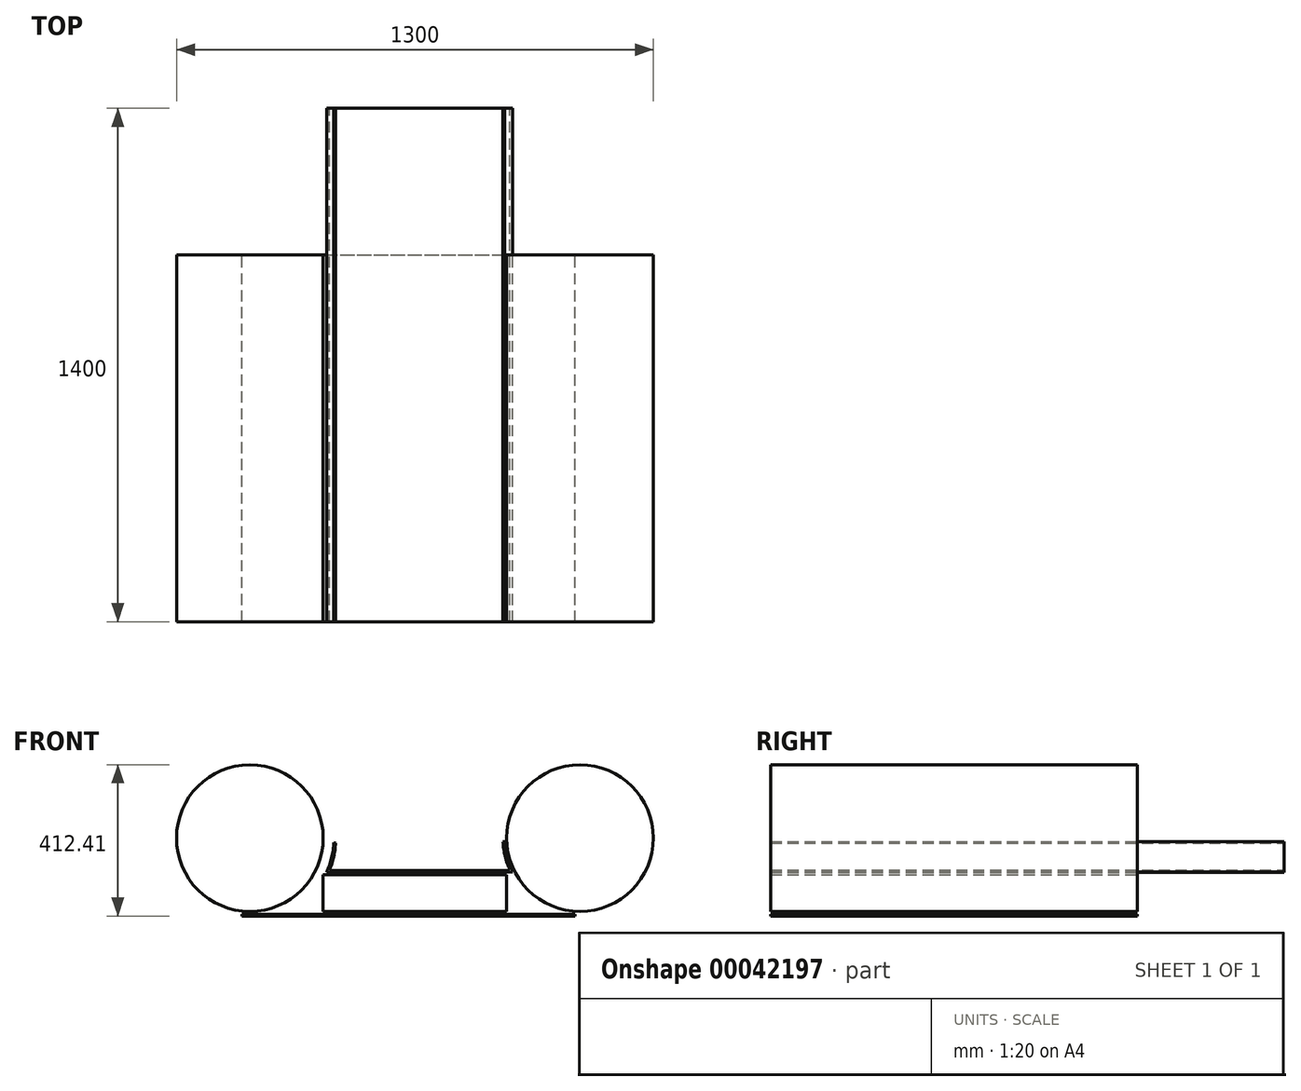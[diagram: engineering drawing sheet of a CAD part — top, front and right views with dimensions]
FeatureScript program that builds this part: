
annotation { "Feature Type Name" : "Feature", "Feature Type Description" : "" }
export const myFeature = defineFeature(function(context is Context, id is Id, definition is map)
    precondition{}
    {
        {
            var Q0;
            Q0=qCreatedBy(makeId("Front.planeOp"),FACE);
            var sketch = newSketch(context, id + "F0", { "sketchPlane" : qUnion([Q0])});
            skCircle(sketch, "E0", {"center": v(-531.07, -125.53) * mm, "radius": 200 * mm});
            skPoint(sketch, "E0.first.point", {"position": v(-686.77, 0) * mm});
            skPoint(sketch, "E0.second.point", {"position": v(-357.87, -225.53) * mm});
            skPoint(sketch, "E0.third.point", {"position": v(-531.07, -325.53) * mm});
            skLineSegment(sketch, "E1.bottom", {"start": v(-331.07, -225.53) * mm, "end": v(168.93, -225.53) * mm});
            skLineSegment(sketch, "E1.top", {"start": v(-331.07, -325.53) * mm, "end": v(168.93, -325.53) * mm});
            skLineSegment(sketch, "E1.left", {"start": v(-331.07, -225.53) * mm, "end": v(-331.07, -325.53) * mm});
            skLineSegment(sketch, "E1.right", {"start": v(168.93, -225.53) * mm, "end": v(168.93, -325.53) * mm});
            skLineSegment(sketch, "E2", {"start": v(-916.77, -325.53) * mm, "end": v(688.73, -325.53) * mm, "construction": true});
            skCircle(sketch, "E3", {"center": v(368.93, -125.53) * mm, "radius": 200 * mm});
            skPoint(sketch, "E3.first.point", {"position": v(267.48, 46.83) * mm});
            skPoint(sketch, "E3.second.point", {"position": v(368.93, -325.53) * mm});
            skPoint(sketch, "E3.third.point", {"position": v(168.93, -225.53) * mm});
            skArc(sketch, "E4", {"start": v(-321.78, -218.91) * mm, "mid": v(-308.32, -179.42) * mm, "end": v(-302.24, -138.14) * mm});
            skArc(sketch, "E5", {"start": v(164.15, -135.08) * mm, "mid": v(170.65, -177.6) * mm, "end": v(185.89, -217.84) * mm});
            skLineSegment(sketch, "E6", {"start": v(-321.78, -218.91) * mm, "end": v(185.89, -217.84) * mm});
            skArc(sketch, "E7.0", {"start": v(-314.2, -213.9) * mm, "mid": v(-302.59, -176.86) * mm, "end": v(-297.25, -138.41) * mm});
            skLineSegment(sketch, "E7.1", {"start": v(-314.2, -213.9) * mm, "end": v(177.94, -212.86) * mm});
            skArc(sketch, "E7.2", {"start": v(159.15, -135.31) * mm, "mid": v(164.83, -174.99) * mm, "end": v(177.94, -212.86) * mm});
            skLineSegment(sketch, "E8", {"start": v(-302.24, -138.14) * mm, "end": v(-297.25, -138.41) * mm});
            skLineSegment(sketch, "E9", {"start": v(159.15, -135.31) * mm, "end": v(164.15, -135.08) * mm});
            skLineSegment(sketch, "E10.bottom", {"start": v(-552.84, -333.33) * mm, "end": v(355.54, -333.33) * mm});
            skLineSegment(sketch, "E10.top", {"start": v(-552.84, -337.94) * mm, "end": v(355.54, -337.94) * mm});
            skLineSegment(sketch, "E10.left", {"start": v(-552.84, -333.33) * mm, "end": v(-552.84, -337.94) * mm});
            skLineSegment(sketch, "E10.right", {"start": v(355.54, -333.33) * mm, "end": v(355.54, -337.94) * mm});
            skSolve(sketch);
        }
        {
            var Q0;
            Q0=makeQuery(id+"F0.imprint","IMPRINT",FACE,{"disambiguationData":[TD([[makeQuery(id+"F0.imprint","IMPRINT",EDGE,{"derivedFrom":sQuery(id+"F0.wireOp",EDGE,"E0")}),1.0]])]});
            var Q1;
            Q1=makeQuery(id+"F0.imprint","IMPRINT",FACE,{"disambiguationData":[TD([[makeQuery(id+"F0.imprint","IMPRINT",EDGE,{"derivedFrom":sQuery(id+"F0.wireOp",EDGE,"E1.bottom")}),-1.0]])]});
            var Q2;
            Q2=makeQuery(id+"F0.imprint","IMPRINT",FACE,{"disambiguationData":[TD([[makeQuery(id+"F0.imprint","IMPRINT",EDGE,{"derivedFrom":sQuery(id+"F0.wireOp",EDGE,"E3")}),1.0]])]});
            var Q3;
            Q3=makeQuery(id+"F0.imprint","IMPRINT",FACE,{"disambiguationData":[TD([[makeQuery(id+"F0.imprint","IMPRINT",EDGE,{"derivedFrom":sQuery(id+"F0.wireOp",EDGE,"E10.bottom")}),-1.0]])]});
            var Q4;
            Q4=makeQuery(id+"F0.imprint","IMPRINT",FACE,{"disambiguationData":[TD([[makeQuery(id+"F0.imprint","IMPRINT",EDGE,{"derivedFrom":sQuery(id+"F0.wireOp",EDGE,"E4")}),-1.0]])]});
            extrude(context, id + "F1", {"entities" : qUnion([Q0, Q1, Q2, Q3, Q4]), "depth" : 1000 * mm});
        }
        {
            var Q0;
            Q0=makeQuery(id+"F1.opExtrude","CAP_FACE",FACE,{"disambiguationData":[OSD([sQuery(id+"F0.wireOp",EDGE,"E4"),sQuery(id+"F0.wireOp",EDGE,"E5"),sQuery(id+"F0.wireOp",EDGE,"E6"),sQuery(id+"F0.wireOp",EDGE,"E7.0"),sQuery(id+"F0.wireOp",EDGE,"E7.1"),sQuery(id+"F0.wireOp",EDGE,"E7.2"),sQuery(id+"F0.wireOp",EDGE,"E8"),sQuery(id+"F0.wireOp",EDGE,"E9")])],"isStart":true});
            extrude(context, id + "F2", {"entities" : qUnion([Q0]), "operationType" : NewBodyOperationType.ADD, "depth" : 400 * mm});
        }
    });
